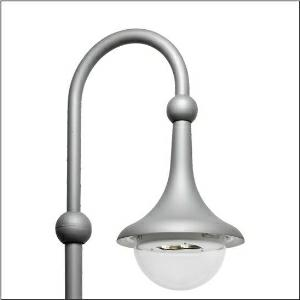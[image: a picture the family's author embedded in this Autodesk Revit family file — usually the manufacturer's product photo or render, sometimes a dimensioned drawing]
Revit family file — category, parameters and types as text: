
# Revit family: grosse_glocke_iq___p1_0a_5xa1565f1f108_f8af
name_source: partatom
category: Lighting Fixtures
units: mm (PartAtom-declared; Revit-internal decimal feet)

## family parameters
Cut with Voids When Loaded = No
Host = Face
Light Source = No
Part Type = Normal
Room Calculation Point = No
Round Connector Dimension = Use Diameter
Shared = No

## types (1)
- --- (1 x LED, 5070 lm, 34.3 W, 3000K)
    Apparent Load = 34 VA
    CIE Flux Codes = 26 57 90 99 100
    Color Rendering = 70
    Color Temperature = 3000K
    Default Elevation = 1800 mm
    Description = Large Bell iQ, mast luminaire, primary light control with 3 zone facetted reflector, of plastic, silver coated, primary optical cover: enclosure, of PMMA, transparent, light distribution: P1.0a, light emission: direct distribution, primary light characteristic: asymmetric, installation type: suspended mounting, High Power LED, rated luminous flux: 5.070lm, luminous efficacy: 148lm/W, light colour: 730, colour temperature: 3000K, control gear: iQ Street-Remote, control: optimised constant luminous flux control (CLO 2.0), Desk-Remote (wireless, voltage-free reading and setting of iQ features in the workshop via application-optimized NFC function/RFID function), Light-Fading, Smart-Wire, Night-Set, Lumen-Switch, Temp-Guard, Auto-Match, Street-Remote, pre-setting: logarithmic dimming characteristic, mains connection: 230..240V, AC, 50/60Hz, start of lifetime: 34W, end of service life: 38W, reduction: 16W, luminaire housing, bell-shaped, of glass-fibre reinforced polyester, coated, Siteco® metallic grey (DB 702S), please order curved mast extension separately, diameter: 530mm, height: 695mm, mounting height: 4..6m, protection rating (complete): IP54, insulation class (complete): insulation class II (safety insulation), certification: CE, ENEC, VDE, impact resistance: IK08, standard-compliant lighting for roads and squares, packaging unit: 1 piece

Light Distribution: P1.0a
    Height = 695 mm
    Lamp = 1 x LED
    Lamp Light Flux = 5070 lm
    Lamp Power = 34.3 W
    Lamp count = 1
    Length = 530 mm
    Luminous efficacy = 148 lm/W
    Manufacturer = Siteco
    ModVariant = No
    Model = 5XA1565F1F108
    Number of Poles = 1
    OnlyDefault = Yes
    Power Factor = 1
    Product Name = Große Glocke iQ | P1.0a
    Product group = mast luminaire | pylon annexe
    ProductGroupID = 6200
    Protection Class = Protection class II
    Protection Degree = IP 54
    RLX_Detail_Level = 1
    RLX_Emergency_Light_Flux = 0 lm
    RLX_Emergency_Type = 0
    RLX_Emergency_Type_DB = No
    RlxData = <blob elided: 53241 chars, md5=830ccea4>
    Socket = socket
    Standby Power = 0 W
    System Light Flux = 5070 lm
    System Power = 34 W
    Type Comments = factory setting: luminous flux: 100 % | dim-lin: 254 | 640 mA
    Type Image = l_1347688.jpg
    URL = http://relux.com
    VarID = @adj_065895
    Voltage = 0 V
    Weight = 0.00 kg
    Width = 0 mm  [stored 0 ft]

note: [stored X ft] marks values corroborated as IEEE doubles in the binary element streams (Revit-internal decimal feet)

## geometry (parser evidence)
native form markers: Blend x4, Sweep x11
no freeform markers — native parametric forms only
